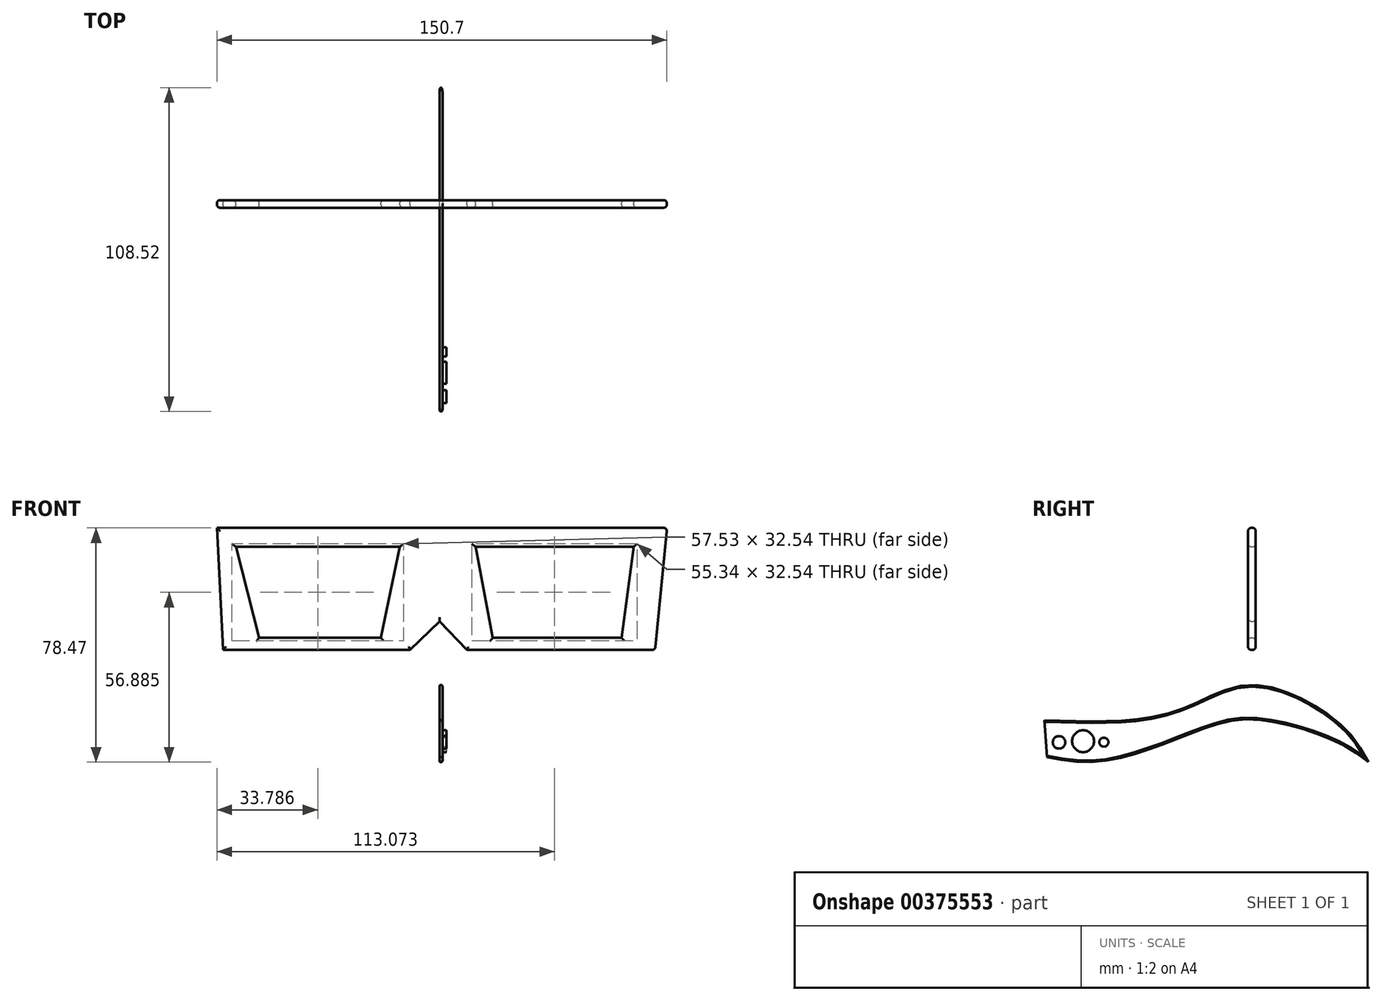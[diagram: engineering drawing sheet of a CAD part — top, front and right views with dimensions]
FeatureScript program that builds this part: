
annotation { "Feature Type Name" : "Feature", "Feature Type Description" : "" }
export const myFeature = defineFeature(function(context is Context, id is Id, definition is map)
    precondition{}
    {
        {
            var Q0;
            Q0=qCreatedBy(makeId("Front.planeOp"),FACE);
            var sketch = newSketch(context, id + "F0", { "sketchPlane" : qUnion([Q0])});
            skLineSegment(sketch, "E0", {"start": v(-74.54, 31.37) * mm, "end": v(76.27, 31.37) * mm});
            skLineSegment(sketch, "E1", {"start": v(0, 0) * mm, "end": v(9.2, -9.5) * mm});
            skLineSegment(sketch, "E2", {"start": v(9.2, -9.5) * mm, "end": v(72.24, -9.5) * mm});
            skLineSegment(sketch, "E3", {"start": v(72.24, -9.5) * mm, "end": v(76.27, 31.37) * mm});
            skLineSegment(sketch, "E4", {"start": v(0, 0) * mm, "end": v(-9.8, -9.5) * mm});
            skLineSegment(sketch, "E5", {"start": v(-9.8, -9.5) * mm, "end": v(-72.53, -9.5) * mm});
            skLineSegment(sketch, "E6", {"start": v(-72.53, -9.5) * mm, "end": v(-74.54, 31.37) * mm});
            skLineSegment(sketch, "E7", {"start": v(-68.2, 25.04) * mm, "end": v(-13.24, 25.04) * mm});
            skLineSegment(sketch, "E8", {"start": v(-13.24, 25.04) * mm, "end": v(-19.57, -5.47) * mm});
            skLineSegment(sketch, "E9", {"start": v(-19.57, -5.47) * mm, "end": v(-60.44, -5.47) * mm});
            skLineSegment(sketch, "E10", {"start": v(-60.44, -5.47) * mm, "end": v(-68.2, 25.04) * mm});
            skLineSegment(sketch, "E11", {"start": v(12.09, 25.04) * mm, "end": v(65.04, 25.04) * mm});
            skLineSegment(sketch, "E12", {"start": v(65.04, 25.04) * mm, "end": v(61.01, -5.47) * mm});
            skLineSegment(sketch, "E13", {"start": v(61.01, -5.47) * mm, "end": v(17.84, -5.47) * mm});
            skLineSegment(sketch, "E14", {"start": v(17.84, -5.47) * mm, "end": v(12.09, 25.04) * mm});
            skSolve(sketch);
        }
        {
            var Q0;
            Q0=makeQuery(id+"F0.imprint","IMPRINT",FACE,{"disambiguationData":[TD([[makeQuery(id+"F0.imprint","IMPRINT",EDGE,{"derivedFrom":sQuery(id+"F0.wireOp",EDGE,"E0")}),-1.0]])]});
            extrude(context, id + "F1", {"entities" : qUnion([Q0]), "depth" : 2.54 * mm});
        }
        {
            var Q0;
            Q0=makeQuery(id+"F1.opExtrude","CAP_EDGE",EDGE,{"disambiguationData":[OSD([sQuery(id+"F0.wireOp",EDGE,"E5")])],"isStart":false});
            var Q1;
            Q1=makeQuery(id+"F1.opExtrude","CAP_EDGE",EDGE,{"disambiguationData":[OSD([sQuery(id+"F0.wireOp",EDGE,"E5")])],"isStart":true});
            var Q2;
            Q2=makeQuery(id+"F1.opExtrude","CAP_EDGE",EDGE,{"disambiguationData":[OSD([sQuery(id+"F0.wireOp",EDGE,"E2")])],"isStart":false});
            var Q3;
            Q3=makeQuery(id+"F1.opExtrude","CAP_EDGE",EDGE,{"disambiguationData":[OSD([sQuery(id+"F0.wireOp",EDGE,"E4")])],"isStart":false});
            var Q4;
            Q4=makeQuery(id+"F1.opExtrude","CAP_EDGE",EDGE,{"disambiguationData":[OSD([sQuery(id+"F0.wireOp",EDGE,"E4")])],"isStart":true});
            var Q5;
            Q5=makeQuery(id+"F1.opExtrude","CAP_EDGE",EDGE,{"disambiguationData":[OSD([sQuery(id+"F0.wireOp",EDGE,"E2")])],"isStart":true});
            var Q6;
            Q6=makeQuery(id+"F1.opExtrude","CAP_EDGE",EDGE,{"disambiguationData":[OSD([sQuery(id+"F0.wireOp",EDGE,"E0")])],"isStart":false});
            var Q7;
            Q7=makeQuery(id+"F1.opExtrude","CAP_EDGE",EDGE,{"disambiguationData":[OSD([sQuery(id+"F0.wireOp",EDGE,"E0")])],"isStart":true});
            var Q8;
            Q8=makeQuery(id+"F1.opExtrude","CAP_EDGE",EDGE,{"disambiguationData":[OSD([sQuery(id+"F0.wireOp",EDGE,"E3")])],"isStart":false});
            var Q9;
            Q9=makeQuery(id+"F1.opExtrude","SWEPT_FACE",FACE,{"disambiguationData":[OSD([sQuery(id+"F0.wireOp",EDGE,"E3")])]});
            var Q10;
            Q10=makeQuery(id+"F1.opExtrude","CAP_EDGE",EDGE,{"disambiguationData":[OSD([sQuery(id+"F0.wireOp",EDGE,"E6")])],"isStart":false});
            var Q11;
            Q11=makeQuery(id+"F1.opExtrude","CAP_EDGE",EDGE,{"disambiguationData":[OSD([sQuery(id+"F0.wireOp",EDGE,"E6")])],"isStart":true});
            var Q12;
            Q12=makeQuery(id+"F1.opExtrude","CAP_EDGE",EDGE,{"disambiguationData":[OSD([sQuery(id+"F0.wireOp",EDGE,"E12")])],"isStart":true});
            var Q13;
            Q13=makeQuery(id+"F1.opExtrude","CAP_EDGE",EDGE,{"disambiguationData":[OSD([sQuery(id+"F0.wireOp",EDGE,"E12")])],"isStart":false});
            var Q14;
            Q14=makeQuery(id+"F1.opExtrude","CAP_EDGE",EDGE,{"disambiguationData":[OSD([sQuery(id+"F0.wireOp",EDGE,"E11")])],"isStart":true});
            var Q15;
            Q15=makeQuery(id+"F1.opExtrude","CAP_EDGE",EDGE,{"disambiguationData":[OSD([sQuery(id+"F0.wireOp",EDGE,"E11")])],"isStart":false});
            var Q16;
            Q16=makeQuery(id+"F1.opExtrude","CAP_EDGE",EDGE,{"disambiguationData":[OSD([sQuery(id+"F0.wireOp",EDGE,"E7")])],"isStart":false});
            var Q17;
            Q17=makeQuery(id+"F1.opExtrude","CAP_EDGE",EDGE,{"disambiguationData":[OSD([sQuery(id+"F0.wireOp",EDGE,"E7")])],"isStart":true});
            var Q18;
            Q18=makeQuery(id+"F1.opExtrude","CAP_EDGE",EDGE,{"disambiguationData":[OSD([sQuery(id+"F0.wireOp",EDGE,"E8")])],"isStart":true});
            var Q19;
            Q19=makeQuery(id+"F1.opExtrude","CAP_EDGE",EDGE,{"disambiguationData":[OSD([sQuery(id+"F0.wireOp",EDGE,"E8")])],"isStart":false});
            var Q20;
            Q20=makeQuery(id+"F1.opExtrude","CAP_EDGE",EDGE,{"disambiguationData":[OSD([sQuery(id+"F0.wireOp",EDGE,"E14")])],"isStart":false});
            var Q21;
            Q21=makeQuery(id+"F1.opExtrude","CAP_EDGE",EDGE,{"disambiguationData":[OSD([sQuery(id+"F0.wireOp",EDGE,"E14")])],"isStart":true});
            var Q22;
            Q22=makeQuery(id+"F1.opExtrude","CAP_EDGE",EDGE,{"disambiguationData":[OSD([sQuery(id+"F0.wireOp",EDGE,"E9")])],"isStart":false});
            var Q23;
            Q23=makeQuery(id+"F1.opExtrude","CAP_EDGE",EDGE,{"disambiguationData":[OSD([sQuery(id+"F0.wireOp",EDGE,"E9")])],"isStart":true});
            var Q24;
            Q24=makeQuery(id+"F1.opExtrude","CAP_EDGE",EDGE,{"disambiguationData":[OSD([sQuery(id+"F0.wireOp",EDGE,"E10")])],"isStart":false});
            var Q25;
            Q25=makeQuery(id+"F1.opExtrude","CAP_EDGE",EDGE,{"disambiguationData":[OSD([sQuery(id+"F0.wireOp",EDGE,"E10")])],"isStart":true});
            var Q26;
            Q26=makeQuery(id+"F1.opExtrude","CAP_EDGE",EDGE,{"disambiguationData":[OSD([sQuery(id+"F0.wireOp",EDGE,"E13")])],"isStart":true});
            var Q27;
            Q27=makeQuery(id+"F1.opExtrude","CAP_EDGE",EDGE,{"disambiguationData":[OSD([sQuery(id+"F0.wireOp",EDGE,"E13")])],"isStart":false});
            var Q28;
            Q28=makeQuery(id+"F1.opExtrude","CAP_EDGE",EDGE,{"disambiguationData":[OSD([sQuery(id+"F0.wireOp",EDGE,"E1")])],"isStart":false});
            var Q29;
            Q29=makeQuery(id+"F1.opExtrude","CAP_EDGE",EDGE,{"disambiguationData":[OSD([sQuery(id+"F0.wireOp",EDGE,"E1")])],"isStart":true});
            fillet(context, id + "F2", {"entities" : qUnion([Q0, Q1, Q2, Q3, Q4, Q5, Q6, Q7, Q8, Q9, Q10, Q11, Q12, Q13, Q14, Q15, Q16, Q17, Q18, Q19, Q20, Q21, Q22, Q23, Q24, Q25, Q26, Q27, Q28, Q29]), "radius" : 1.02 * mm, "tangentPropagation" : true, "allowEdgeOverflow" : false});
        }
        {
            var Q0;
            Q0=qCreatedBy(makeId("Right.planeOp"),FACE);
            var sketch = newSketch(context, id + "F3", { "sketchPlane" : qUnion([Q0])});
            skFitSpline(sketch, "E15", {"points": [v(-69.94, -45.47) * mm, v(-50.08, -46.62) * mm, v(-19.28, -36.55) * mm, v(0, -32.8) * mm, v(27.05, -40.3) * mm, v(37.7, -46.91) * mm], "startDerivative": vector(96.58, -18.1) * mm, "endDerivative": vector(58.08, -43.32) * mm});
            skFitSpline(sketch, "E16", {"points": [v(-70.8, -33.1) * mm, v(-43.17, -33.1) * mm, v(-22.74, -28.5) * mm, v(0, -21.3) * mm, v(29.07, -35.11) * mm, v(37.7, -46.91) * mm], "startDerivative": vector(132.47, -4.43) * mm, "endDerivative": vector(38.84, -72.12) * mm});
            skFitSpline(sketch, "E17", {"points": [v(-70.8, -33.1) * mm, v(-69.94, -45.47) * mm], "startDerivative": vector(0.86, -12.38) * mm, "endDerivative": vector(0.86, -12.38) * mm});
            skSolve(sketch);
        }
        {
            var Q0;
            Q0=makeQuery(id+"F3.imprint","IMPRINT",FACE,{"disambiguationData":[TD([[makeQuery(id+"F3.imprint","IMPRINT",EDGE,{"derivedFrom":sQuery(id+"F3.wireOp",EDGE,"E15")}),1.0]])]});
            extrude(context, id + "F4", {"entities" : qUnion([Q0]), "depth" : 1.02 * mm});
        }
        {
            var Q0;
            Q0=makeQuery(id+"F4.opExtrude","CAP_EDGE",EDGE,{"disambiguationData":[OSD([sQuery(id+"F3.wireOp",EDGE,"E16")])],"isStart":false});
            var Q1;
            Q1=makeQuery(id+"F4.opExtrude","CAP_EDGE",EDGE,{"disambiguationData":[OSD([sQuery(id+"F3.wireOp",EDGE,"E15")])],"isStart":false});
            var Q2;
            Q2=makeQuery(id+"F4.opExtrude","CAP_EDGE",EDGE,{"disambiguationData":[OSD([sQuery(id+"F3.wireOp",EDGE,"E17")])],"isStart":false});
            var Q3;
            Q3=makeQuery(id+"F4.opExtrude","CAP_EDGE",EDGE,{"disambiguationData":[OSD([sQuery(id+"F3.wireOp",EDGE,"E15")])],"isStart":true});
            var Q4;
            Q4=makeQuery(id+"F4.opExtrude","CAP_EDGE",EDGE,{"disambiguationData":[OSD([sQuery(id+"F3.wireOp",EDGE,"E17")])],"isStart":true});
            var Q5;
            Q5=makeQuery(id+"F4.opExtrude","CAP_EDGE",EDGE,{"disambiguationData":[OSD([sQuery(id+"F3.wireOp",EDGE,"E16")])],"isStart":true});
            fillet(context, id + "F5", {"entities" : qUnion([Q0, Q1, Q2, Q3, Q4, Q5]), "radius" : 0.5 * mm, "tangentPropagation" : true, "allowEdgeOverflow" : false});
        }
        {
            var Q0;
            Q0=makeQuery(id+"F4.opExtrude","CAP_FACE",FACE,{"disambiguationData":[OSD([sQuery(id+"F3.wireOp",EDGE,"E15"),sQuery(id+"F3.wireOp",EDGE,"E16"),sQuery(id+"F3.wireOp",EDGE,"E17")])],"isStart":false});
            var sketch = newSketch(context, id + "F6", { "sketchPlane" : qUnion([Q0])});
            skCircle(sketch, "E18", {"center": v(-65.84, -40.48) * mm, "radius": 2.1 * mm});
            skCircle(sketch, "E19", {"center": v(-57.81, -40.1) * mm, "radius": 3.67 * mm});
            skCircle(sketch, "E20", {"center": v(-50.84, -40.42) * mm, "radius": 1.52 * mm});
            skSolve(sketch);
        }
        {
            var Q0;
            Q0=makeQuery(id+"F6.imprint","IMPRINT",FACE,{"disambiguationData":[TD([[makeQuery(id+"F6.imprint","IMPRINT",EDGE,{"derivedFrom":sQuery(id+"F6.wireOp",EDGE,"E19")}),1.0]])]});
            var Q1;
            Q1=makeQuery(id+"F6.imprint","IMPRINT",FACE,{"disambiguationData":[TD([[makeQuery(id+"F6.imprint","IMPRINT",EDGE,{"derivedFrom":sQuery(id+"F6.wireOp",EDGE,"E18")}),1.0]])]});
            var Q2;
            Q2=makeQuery(id+"F6.imprint","IMPRINT",FACE,{"disambiguationData":[TD([[makeQuery(id+"F6.imprint","IMPRINT",EDGE,{"derivedFrom":sQuery(id+"F6.wireOp",EDGE,"E20")}),1.0]])]});
            extrude(context, id + "F7", {"entities" : qUnion([Q0, Q1, Q2]), "operationType" : NewBodyOperationType.ADD, "depth" : 1.27 * mm});
        }
    });
